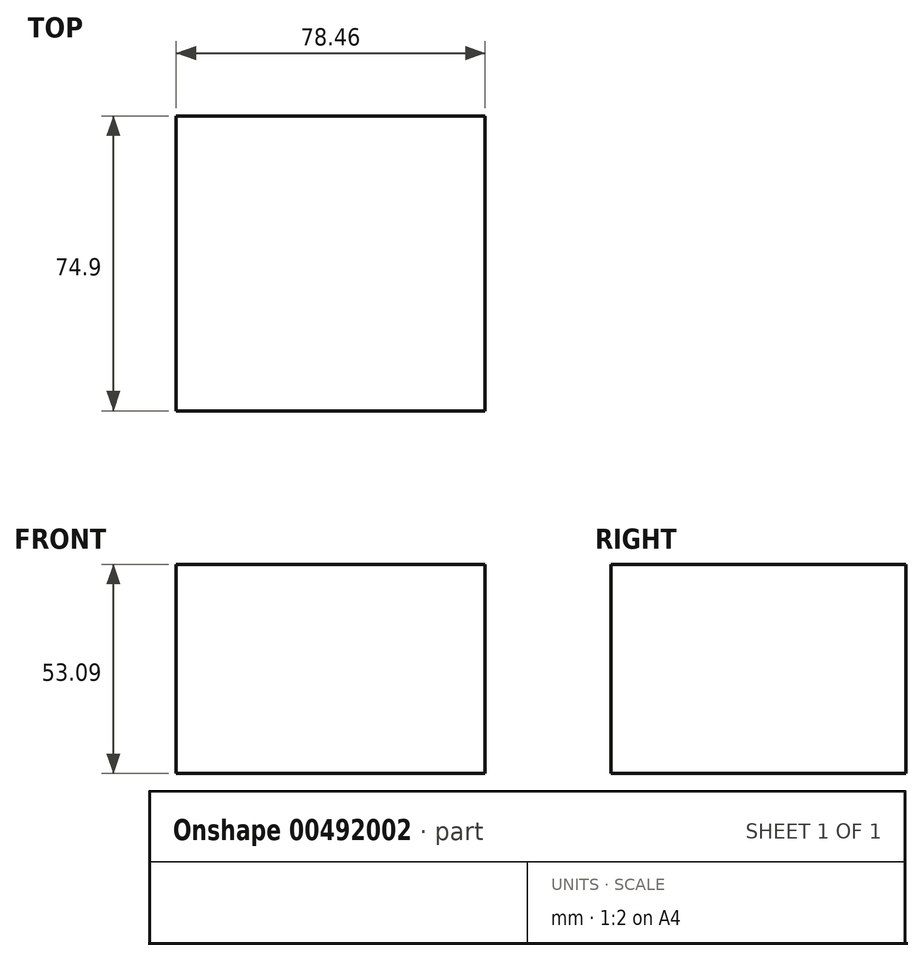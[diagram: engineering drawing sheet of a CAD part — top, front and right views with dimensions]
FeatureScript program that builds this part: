
annotation { "Feature Type Name" : "Feature", "Feature Type Description" : "" }
export const myFeature = defineFeature(function(context is Context, id is Id, definition is map)
    precondition{}
    {
        {
            var Q0;
            Q0=qCreatedBy(makeId("Top.planeOp"),FACE);
            var sketch = newSketch(context, id + "F0", { "sketchPlane" : qUnion([Q0])});
            skLineSegment(sketch, "E0.bottom", {"start": v(33.88, -32.55) * mm, "end": v(-44.58, -32.55) * mm});
            skLineSegment(sketch, "E0.top", {"start": v(33.88, 42.35) * mm, "end": v(-44.58, 42.35) * mm});
            skLineSegment(sketch, "E0.left", {"start": v(33.88, -32.55) * mm, "end": v(33.88, 42.35) * mm});
            skLineSegment(sketch, "E0.right", {"start": v(-44.58, -32.55) * mm, "end": v(-44.58, 42.35) * mm});
            skPoint(sketch, "E0.middle", {"position": v(-5.35, 4.9) * mm});
            skSolve(sketch);
        }
        {
            var Q0;
            Q0 = qSketchRegion(id + "F0", true);
            extrude(context, id + "F1", {"entities" : qUnion([Q0]), "depth" : 53.1 * mm});
        }
    });
